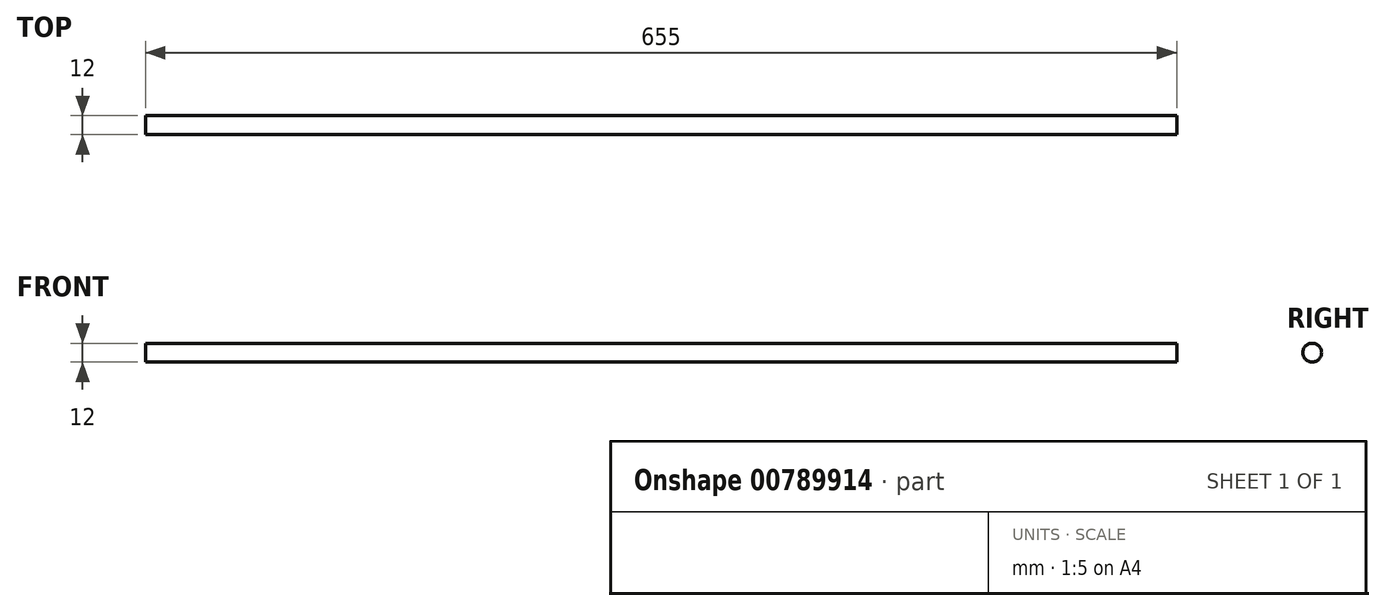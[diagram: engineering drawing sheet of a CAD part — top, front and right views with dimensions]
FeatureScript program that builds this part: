
annotation { "Feature Type Name" : "Feature", "Feature Type Description" : "" }
export const myFeature = defineFeature(function(context is Context, id is Id, definition is map)
    precondition{}
    {
        {
            var Q0;
            Q0=qCreatedBy(makeId("Right.planeOp"),FACE);
            var sketch = newSketch(context, id + "F0", { "sketchPlane" : qUnion([Q0])});
            skCircle(sketch, "E0", {"center": v(0, 0) * mm, "radius": 6 * mm});
            skSolve(sketch);
        }
        {
            var Q0;
            Q0=qSketchRegion(id+"F0",true);
            extrude(context, id + "F1", {"entities" : qUnion([Q0]), "depth" : 327.5 * mm, "offsetDistance" : 25 * mm, "hasSecondDirection" : true, "secondDirectionOppositeDirection" : true, "secondDirectionDepth" : 327.5 * mm});
        }
    });
